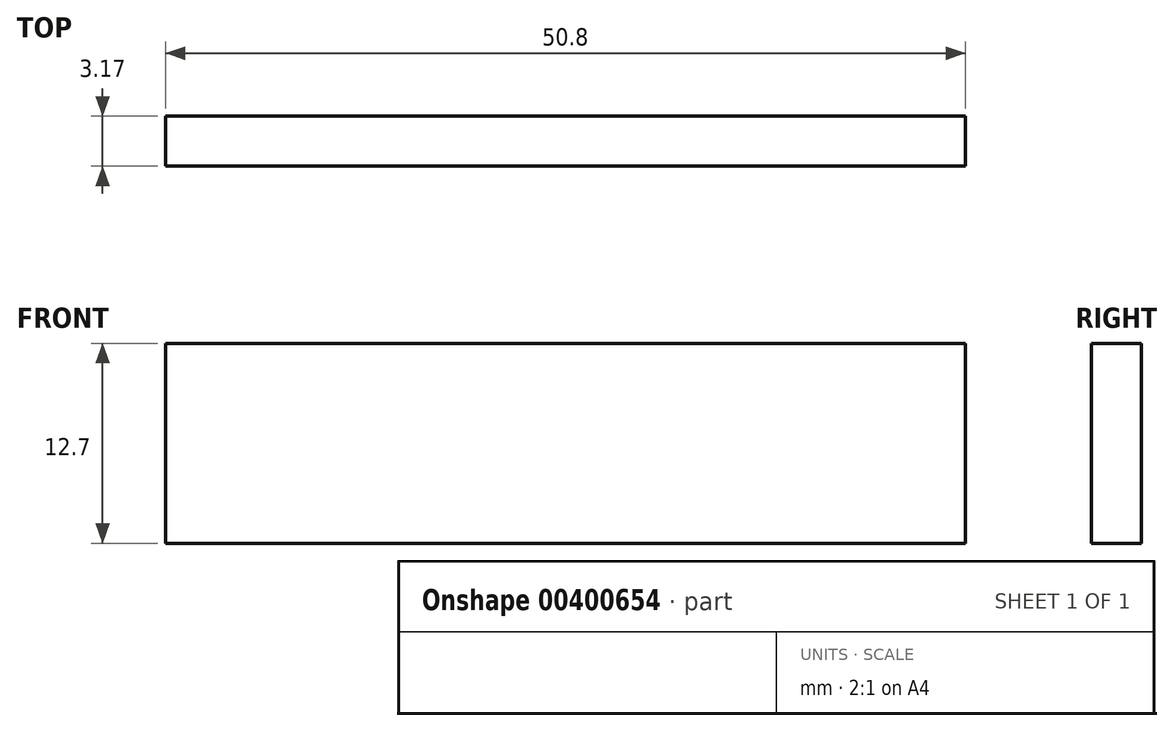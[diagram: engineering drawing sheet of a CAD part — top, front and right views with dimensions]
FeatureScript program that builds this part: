
annotation { "Feature Type Name" : "Feature", "Feature Type Description" : "" }
export const myFeature = defineFeature(function(context is Context, id is Id, definition is map)
    precondition{}
    {
        {
            var Q0;
            Q0=qCreatedBy(makeId("Front.planeOp"),FACE);
            var sketch = newSketch(context, id + "F0", { "sketchPlane" : qUnion([Q0])});
            skLineSegment(sketch, "E0.bottom", {"start": v(7.56, 39.66) * mm, "end": v(58.36, 39.66) * mm});
            skLineSegment(sketch, "E0.top", {"start": v(7.56, 26.96) * mm, "end": v(58.36, 26.96) * mm});
            skLineSegment(sketch, "E0.left", {"start": v(7.56, 39.66) * mm, "end": v(7.56, 26.96) * mm});
            skLineSegment(sketch, "E0.right", {"start": v(58.36, 39.66) * mm, "end": v(58.36, 26.96) * mm});
            skSolve(sketch);
        }
        {
            var Q0;
            Q0=makeQuery(id+"F0.imprint","IMPRINT",FACE,{"disambiguationData":[TD([[makeQuery(id+"F0.imprint","IMPRINT",EDGE,{"derivedFrom":sQuery(id+"F0.wireOp",EDGE,"E0.bottom")}),-1.0]])]});
            extrude(context, id + "F1", {"entities" : qUnion([Q0]), "depth" : 3.17 * mm});
        }
    });
